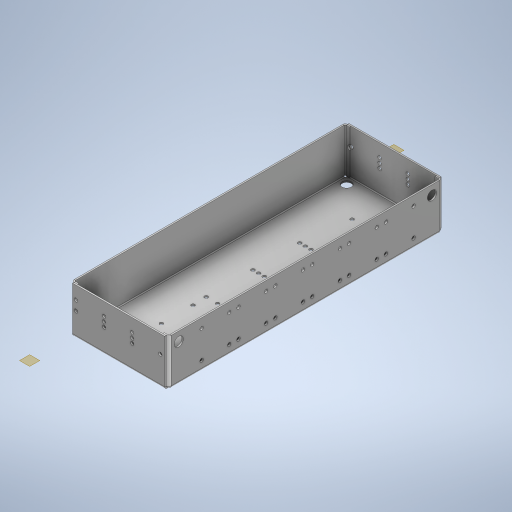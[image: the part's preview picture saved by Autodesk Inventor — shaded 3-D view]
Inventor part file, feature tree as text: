
AUTODESK INVENTOR PART (.ipt)
format: ipt  version: 2023 (Build 270158000, 158)  size: 652,800 bytes
history: native  units: in
note: dims shown in document units (in); Inventor stores cm internally (conversion verified against a paired STEP export)
features: sketch x17, hole x13, sheet_metal_op x12, pattern_linear x8, other x6, plane x4
ambient origin geometry x8: Origin, YZ Plane, XZ Plane, XY Plane, X Axis, Y Axis, Z Axis, Center Point
bodies: Solid1 (feature_tree)
feature tree (60):
  sheet_metal_op  "Face1"
  sheet_metal_op  "Flange1"
  sheet_metal_op  "Flange2"
  sheet_metal_op  "Unfold1"
  hole  "Hole1"  [1 undecoded]
  pattern_linear  "Rectangular Pattern1"  Count1=30  [1 undecoded]
  pattern_linear  "Rectangular Pattern2"  Count1=10  [1 undecoded]
  hole  "Hole2"  [1 undecoded]
  pattern_linear  "Rectangular Pattern3"  Count1=10 Spacing1=90.0deg
  hole  "Hole3"  [1 undecoded]
  hole  "Hole6"  [1 undecoded]
  pattern_linear  "Rectangular Pattern6"  Count1=10 Spacing1=90.0deg
  plane  "Work Plane4"
  hole  "Hole7"  [1 undecoded]
  plane  "Work Plane3"
  hole  "Hole8"  [1 undecoded]
  plane  "Work Plane2"
  hole  "Hole9"  [1 undecoded]
  plane  "Work Plane1"
  hole  "Hole10"  [1 undecoded]
  hole  "Hole11"  [1 undecoded]
  hole  "Hole12"  [1 undecoded]
  hole  "Hole13"  [1 undecoded]
  pattern_linear  "Rectangular Pattern11"  Spacing1=0.8108in  [1 undecoded]
  pattern_linear  "Rectangular Pattern12"  Count1=6  [1 undecoded]
  pattern_linear  "Rectangular Pattern13"  Count1=6  [1 undecoded]
  pattern_linear  "Rectangular Pattern14"  Count1=6  [1 undecoded]
  sheet_metal_op  "Refold6"
  sheet_metal_op  "Flange8"
  hole  "Hole14"  [1 undecoded]
  hole  "Hole15"  [1 undecoded]
  sketch  "Sketch1"  dims[d0=23.622in d1=7.874in d2=11.811in d3=3.937in]
  other  "Plate1"
  sketch  "Sketch2"  dims[d4=0.125in d5=0.125in]
  other  "Plate2"
  sheet_metal_op  "Bend1"
  sheet_metal_op  "Corner1"
  sketch  "Sketch3"  dims[d6=0.0625in]
  other  "Plate3"
  sheet_metal_op  "Bend2"
  sheet_metal_op  "Corner2"
  sketch  "Sketch5"  dims[d7=0.25in]
  sketch  "Sketch6"  dims[d8=0.125in d9=3.937in d10=90.0deg d11=0.0787in]
  sketch  "Sketch7"  dims[d12=0.5in d13=0.125in]
  sketch  "Sketch10"  dims[d14=0.125in d15=0.125in]
  sketch  "Sketch11"  dims[d16=0.0625in]
  sketch  "Sketch13"  dims[d17=0.25in]
  sketch  "Sketch15"  dims[d18=0.125in d19=3.937in d20=90.0deg d21=0.0787in]
  sketch  "Sketch16"  dims[d22=0.5in d23=0.125in]
  sketch  "Sketch17"  dims[d24=0.125in]
  sketch  "Sketch21"  dims[d35=0.2969in d36=0.2953in d37=0.1476in d38=0.0984in d39=90.0deg d40=0.12in d41=0.8108in]
  sketch  "Sketch25"  dims[d42=0.7874in d44=0.9646in d46=1.1811in d48=3.9921in]
  sketch  "Sketch26"  dims[d49=0.2969in d50=0.2953in d51=0.1476in d52=0.0984in d53=90.0deg d54=0.3937in d55=0.8108in d56=0.9646in]
  other  "Plate9"
  sheet_metal_op  "Bend8"
  sheet_metal_op  "Corner8"
  sketch  "Sketch27"  dims[d57=0.9646in d58=0.4823in]
  sketch  "Sketch28"  dims[d59=1.1811in d61=3.9921in d62=0.7874in d63=0.2953in d64=0.1476in d65=0.0984in d66=90.0deg d67=0.3937in d68=0.8108in d69=0.5906in d70=0.5906in d95=0.2969in d96=0.2953in d97=0.1476in d98=0.0984in d99=90.0deg d100=0.12in d101=0.8108in d102=2.3622in d103=2.3622in d104=2.3622in d105=0.7874in d106=2.3622in d107=2.3622in d109=3.1496in d110=0.2969in d111=0.2953in d112=0.1476in d113=0.0984in d114=90.0deg d115=0.12in d116=0.8108in d122=0.2969in d123=0.2953in d124=0.1476in d125=0.0984in d126=90.0deg d127=0.3937in d128=0.8108in d129=0.8071in d130=0.4035in d134=0.2969in d135=0.2953in d136=0.1476in d137=0.0984in d138=90.0deg d139=0.3937in d140=0.8108in d144=0.2969in d145=0.2953in d146=0.1476in d147=0.0984in d148=90.0deg d149=0.3937in d150=0.8108in d151=0.8071in d158=0.2969in d159=0.2953in d160=0.1476in d161=0.0984in d162=90.0deg d163=0.3937in d164=0.8108in d165=1.9252in d166=2.6949in d167=1.1811in d168=0.9626in d169=0.7874in d170=0.2953in d171=0.1476in d172=0.0984in d173=90.0deg d174=0.3937in d175=0.8108in d176=0.7874in d177=0.2953in d178=0.1476in d179=0.0984in d180=90.0deg d181=0.3937in d182=0.8108in d183=0.7874in d184=0.7874in d185=0.7874in d186=0.7874in d188=0.374in d189=2.433in d190=0.3346in d191=2.433in d192=1.1811in d194=2.4016in d195=1.1811in d197=2.4016in d198=1.1811in d200=2.4016in d201=1.1811in d203=2.4016in d205=8.6614in d206=0.5316in d231=0.0984in d238=0.0433in d250=0.0787in d263=0.0472in d265=0.0472in d270=0.0354in d271=0.125in d272=0.0in d273=0.125in d274=0.0in d275=0.125in d276=0.0625in d277=0.25in d278=0.125in d279=0.4921in d280=90.0deg d281=0.0984in d282=0.5in d283=0.125in d284=0.125in d285=7.874in d286=2.4016in d287=0.4331in d288=0.2953in d289=0.1476in d290=0.0984in d291=90.0deg d292=0.12in d293=0.0in d294=0.4331in d295=0.2953in d296=0.1476in d297=0.0984in d298=90.0deg d299=0.3937in d300=0.0in]
  other  "Cut4"
  other  "Cut5"
note: 19 required parameter values undecoded (feature->parameter linkage not recoverable at this tier; creation-order binding heuristic only, values carry confidence <= 0.55)
